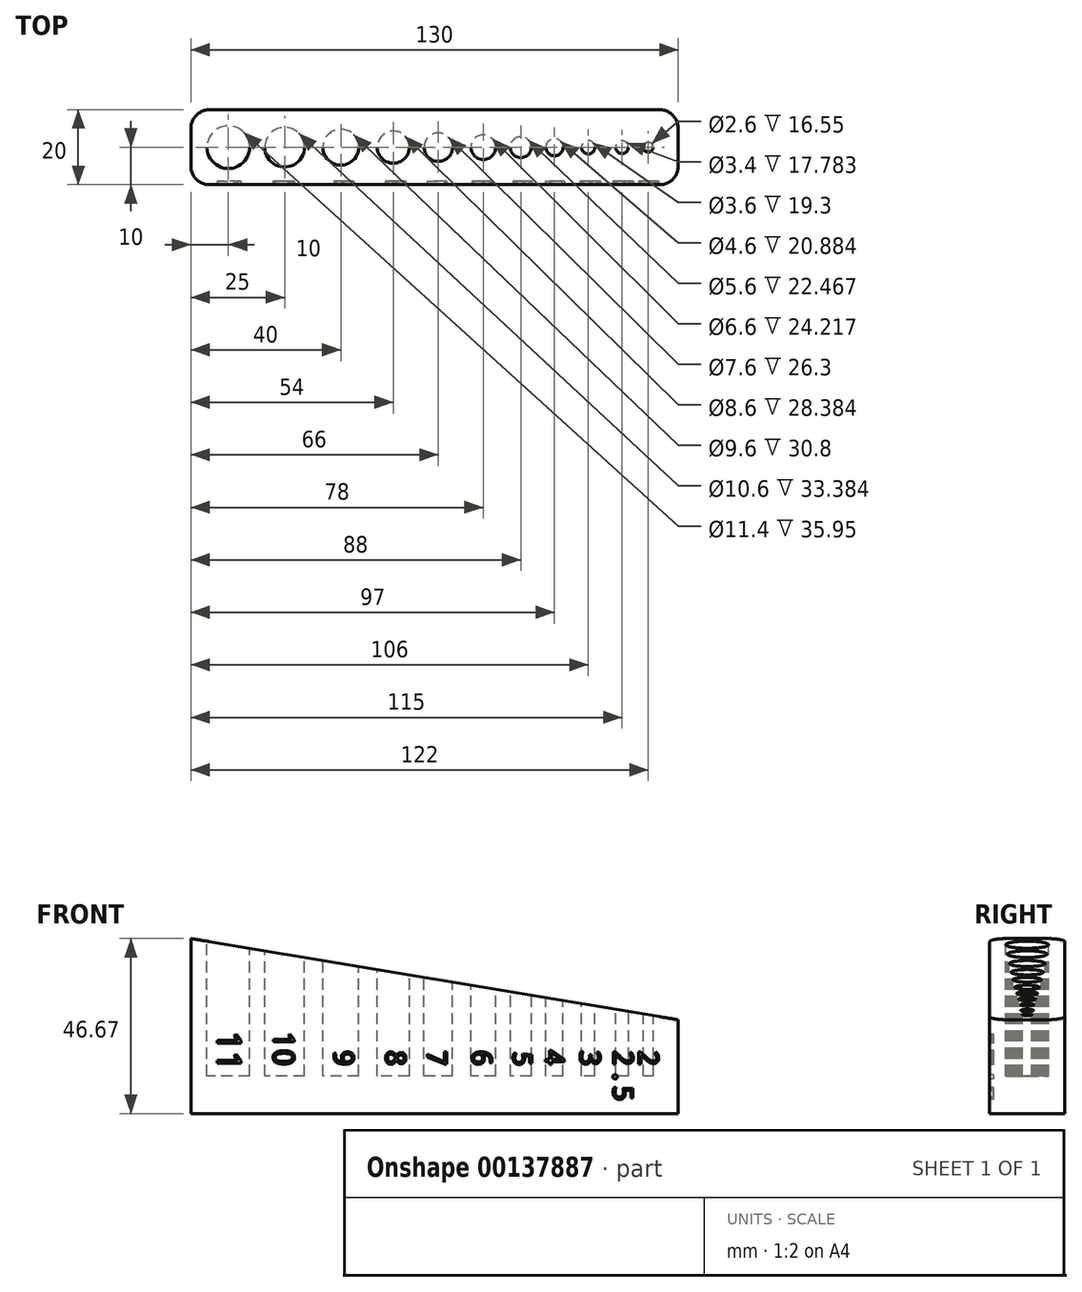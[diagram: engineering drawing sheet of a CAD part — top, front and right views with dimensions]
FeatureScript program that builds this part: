
annotation { "Feature Type Name" : "Feature", "Feature Type Description" : "" }
export const myFeature = defineFeature(function(context is Context, id is Id, definition is map)
    precondition{}
    {
        {
            var Q0;
            Q0=qCreatedBy(makeId("Top.planeOp"),FACE);
            var sketch = newSketch(context, id + "F0", { "sketchPlane" : qUnion([Q0])});
            skLineSegment(sketch, "E0.bottom", {"start": v(65, 10) * mm, "end": v(-65, 10) * mm});
            skLineSegment(sketch, "E0.top", {"start": v(65, -10) * mm, "end": v(-65, -10) * mm});
            skLineSegment(sketch, "E0.left", {"start": v(65, 10) * mm, "end": v(65, -10) * mm});
            skLineSegment(sketch, "E0.right", {"start": v(-65, 10) * mm, "end": v(-65, -10) * mm});
            skPoint(sketch, "E0.middle", {"position": v(0, 0) * mm});
            skSolve(sketch);
        }
        {
            var Q0;
            Q0=makeQuery(id+"F0.imprint","IMPRINT",FACE,{"disambiguationData":[TD([[makeQuery(id+"F0.imprint","IMPRINT",EDGE,{"derivedFrom":sQuery(id+"F0.wireOp",EDGE,"E0.bottom")}),1.0]])]});
            extrude(context, id + "F1", {"entities" : qUnion([Q0]), "depth" : 50 * mm});
        }
        {
            var Q0;
            Q0=makeQuery(id+"F1.opExtrude","CAP_FACE",FACE,{"disambiguationData":[OSD([sQuery(id+"F0.wireOp",EDGE,"E0.bottom"),sQuery(id+"F0.wireOp",EDGE,"E0.top"),sQuery(id+"F0.wireOp",EDGE,"E0.left"),sQuery(id+"F0.wireOp",EDGE,"E0.right")])],"isStart":false});
            var sketch = newSketch(context, id + "F2", { "sketchPlane" : qUnion([Q0])});
            skPoint(sketch, "E1", {"position": v(-55, 0) * mm});
            skCircle(sketch, "E2", {"center": v(-55, 0) * mm, "radius": 5.7 * mm});
            skCircle(sketch, "E3", {"center": v(-40, 0) * mm, "radius": 5.3 * mm});
            skCircle(sketch, "E4", {"center": v(-25, 0) * mm, "radius": 4.8 * mm});
            skCircle(sketch, "E5", {"center": v(-11, 0) * mm, "radius": 4.3 * mm});
            skCircle(sketch, "E6", {"center": v(1, 0) * mm, "radius": 3.8 * mm});
            skCircle(sketch, "E7", {"center": v(13, 0) * mm, "radius": 3.3 * mm});
            skCircle(sketch, "E8", {"center": v(23, 0) * mm, "radius": 2.8 * mm});
            skCircle(sketch, "E9", {"center": v(32, 0) * mm, "radius": 2.3 * mm});
            skCircle(sketch, "E10", {"center": v(41, 0) * mm, "radius": 1.8 * mm});
            skCircle(sketch, "E11", {"center": v(50, 0) * mm, "radius": 1.7 * mm});
            skCircle(sketch, "E12", {"center": v(57, 0) * mm, "radius": 1.3 * mm});
            skSolve(sketch);
        }
        {
            var Q0;
            Q0=makeQuery(id+"F2.imprint","IMPRINT",FACE,{"disambiguationData":[TD([[makeQuery(id+"F2.imprint","IMPRINT",EDGE,{"derivedFrom":sQuery(id+"F2.wireOp",EDGE,"E2")}),1.0]])]});
            var Q1;
            Q1=makeQuery(id+"F2.imprint","IMPRINT",FACE,{"disambiguationData":[TD([[makeQuery(id+"F2.imprint","IMPRINT",EDGE,{"derivedFrom":sQuery(id+"F2.wireOp",EDGE,"E3")}),1.0]])]});
            var Q2;
            Q2=makeQuery(id+"F2.imprint","IMPRINT",FACE,{"disambiguationData":[TD([[makeQuery(id+"F2.imprint","IMPRINT",EDGE,{"derivedFrom":sQuery(id+"F2.wireOp",EDGE,"E4")}),1.0]])]});
            var Q3;
            Q3=makeQuery(id+"F2.imprint","IMPRINT",FACE,{"disambiguationData":[TD([[makeQuery(id+"F2.imprint","IMPRINT",EDGE,{"derivedFrom":sQuery(id+"F2.wireOp",EDGE,"E5")}),1.0]])]});
            var Q4;
            Q4=makeQuery(id+"F2.imprint","IMPRINT",FACE,{"disambiguationData":[TD([[makeQuery(id+"F2.imprint","IMPRINT",EDGE,{"derivedFrom":sQuery(id+"F2.wireOp",EDGE,"E6")}),1.0]])]});
            var Q5;
            Q5=makeQuery(id+"F2.imprint","IMPRINT",FACE,{"disambiguationData":[TD([[makeQuery(id+"F2.imprint","IMPRINT",EDGE,{"derivedFrom":sQuery(id+"F2.wireOp",EDGE,"E7")}),1.0]])]});
            var Q6;
            Q6=makeQuery(id+"F2.imprint","IMPRINT",FACE,{"disambiguationData":[TD([[makeQuery(id+"F2.imprint","IMPRINT",EDGE,{"derivedFrom":sQuery(id+"F2.wireOp",EDGE,"E8")}),1.0]])]});
            var Q7;
            Q7=makeQuery(id+"F2.imprint","IMPRINT",FACE,{"disambiguationData":[TD([[makeQuery(id+"F2.imprint","IMPRINT",EDGE,{"derivedFrom":sQuery(id+"F2.wireOp",EDGE,"E9")}),1.0]])]});
            var Q8;
            Q8=makeQuery(id+"F2.imprint","IMPRINT",FACE,{"disambiguationData":[TD([[makeQuery(id+"F2.imprint","IMPRINT",EDGE,{"derivedFrom":sQuery(id+"F2.wireOp",EDGE,"E10")}),1.0]])]});
            var Q9;
            Q9=makeQuery(id+"F2.imprint","IMPRINT",FACE,{"disambiguationData":[TD([[makeQuery(id+"F2.imprint","IMPRINT",EDGE,{"derivedFrom":sQuery(id+"F2.wireOp",EDGE,"E11")}),1.0]])]});
            var Q10;
            Q10=makeQuery(id+"F2.imprint","IMPRINT",FACE,{"disambiguationData":[TD([[makeQuery(id+"F2.imprint","IMPRINT",EDGE,{"derivedFrom":sQuery(id+"F2.wireOp",EDGE,"E12")}),1.0]])]});
            extrude(context, id + "F3", {"entities" : qUnion([Q0, Q1, Q2, Q3, Q4, Q5, Q6, Q7, Q8, Q9, Q10]), "operationType" : NewBodyOperationType.REMOVE, "oppositeDirection" : true, "depth" : 40 * mm});
        }
        {
            var Q0;
            Q0=makeQuery(id+"F1.opExtrude","CAP_EDGE",EDGE,{"disambiguationData":[OSD([sQuery(id+"F0.wireOp",EDGE,"E0.left")])],"isStart":false});
            chamfer(context, id + "F4", {"entities" : qUnion([Q0]), "chamferType" : ChamferType.TWO_OFFSETS, "width1" : 25 * mm, "oppositeDirection" : false, "width2" : 150 * mm, "tangentPropagation" : true});
        }
        {
            var Q0;
            Q0=makeQuery(id+"F1.opExtrude","SWEPT_EDGE",EDGE,{"disambiguationData":[OSD([sQuery(id+"F0.wireOp",EDGE,"E0.top"),sQuery(id+"F0.wireOp",EDGE,"E0.right")])]});
            var Q1;
            Q1=makeQuery(id+"F1.opExtrude","SWEPT_EDGE",EDGE,{"disambiguationData":[OSD([sQuery(id+"F0.wireOp",EDGE,"E0.bottom"),sQuery(id+"F0.wireOp",EDGE,"E0.right")])]});
            var Q2;
            Q2=makeQuery(id+"F1.opExtrude","SWEPT_EDGE",EDGE,{"disambiguationData":[OSD([sQuery(id+"F0.wireOp",EDGE,"E0.bottom"),sQuery(id+"F0.wireOp",EDGE,"E0.left")])]});
            var Q3;
            Q3=makeQuery(id+"F1.opExtrude","SWEPT_EDGE",EDGE,{"disambiguationData":[OSD([sQuery(id+"F0.wireOp",EDGE,"E0.top"),sQuery(id+"F0.wireOp",EDGE,"E0.left")])]});
            fillet(context, id + "F5", {"entities" : qUnion([Q0, Q1, Q2, Q3]), "radius" : 5 * mm, "tangentPropagation" : true, "allowEdgeOverflow" : false});
        }
        {
            var Q0;
            Q0=makeQuery(id+"F1.opExtrude","SWEPT_FACE",FACE,{"disambiguationData":[OSD([sQuery(id+"F0.wireOp",EDGE,"E0.top")])]});
            var sketch = newSketch(context, id + "F6", { "sketchPlane" : qUnion([Q0])});
            skLineSegment(sketch, "E13", {"start": v(-77.65, 10) * mm, "end": v(102.7, 10) * mm, "construction": true});
            skText(sketch, "E14", { "text": "10", "fontName": "DroidSansMono.ttf"});
            skText(sketch, "E15", { "text": "11", "fontName": "DroidSansMono.ttf"});
            skPoint(sketch, "E15.firstSnap0", {"position": v(-40.18, 25.98) * mm});
            skText(sketch, "E16", { "text": "9", "fontName": "DroidSansMono.ttf"});
            skText(sketch, "E17", { "text": "8", "fontName": "DroidSansMono.ttf"});
            skText(sketch, "E18", { "text": "7", "fontName": "DroidSansMono.ttf"});
            skText(sketch, "E19", { "text": "6", "fontName": "DroidSansMono.ttf"});
            skText(sketch, "E20", { "text": "5", "fontName": "DroidSansMono.ttf"});
            skText(sketch, "E21", { "text": "4", "fontName": "DroidSansMono.ttf"});
            skText(sketch, "E22", { "text": "3", "fontName": "DroidSansMono.ttf"});
            skText(sketch, "E23", { "text": "2", "fontName": "DroidSansMono.ttf"});
            skText(sketch, "E24", { "text": "2", "fontName": "DroidSansMono.ttf"});
            skText(sketch, "E25", { "text": ".5", "fontName": "DroidSansMono.ttf"});
            const initialGuessF6  = {"E14": [-0.043, 0.022, 0, -1, 0.00563], "E15": [-0.058, 0.02211, 0, -1, 0.00643], "E16": [-0.02683, 0.017, 0, -1, 0.00533], "E17": [-0.013, 0.017, 0, -1, 0.00534], "E18": [-0.002, 0.017, 0, -1, 0.0053], "E19": [0.01, 0.017, 0, -1, 0.00533], "E20": [0.021, 0.01662, 0, -1, 0.005], "E21": [0.0295, 0.017, 0, -1, 0.00514], "E22": [0.03882, 0.017, 0, -1, 0.00541], "E23": [0.0544, 0.017, 0, -1, 0.00536], "E24": [0.04764, 0.017, 0, -1, 0.00536], "E25": [0.04768, 0.012, 0, -1, 0.00532]};
            skSetInitialGuess(sketch, initialGuessF6);
            skSolve(sketch);
        }
        {
            var Q0;
            Q0 = qSketchRegion(id + "F6", true);
            extrude(context, id + "F7", {"entities" : qUnion([Q0]), "operationType" : NewBodyOperationType.REMOVE, "oppositeDirection" : true, "depth" : 1 * mm});
        }
    });
